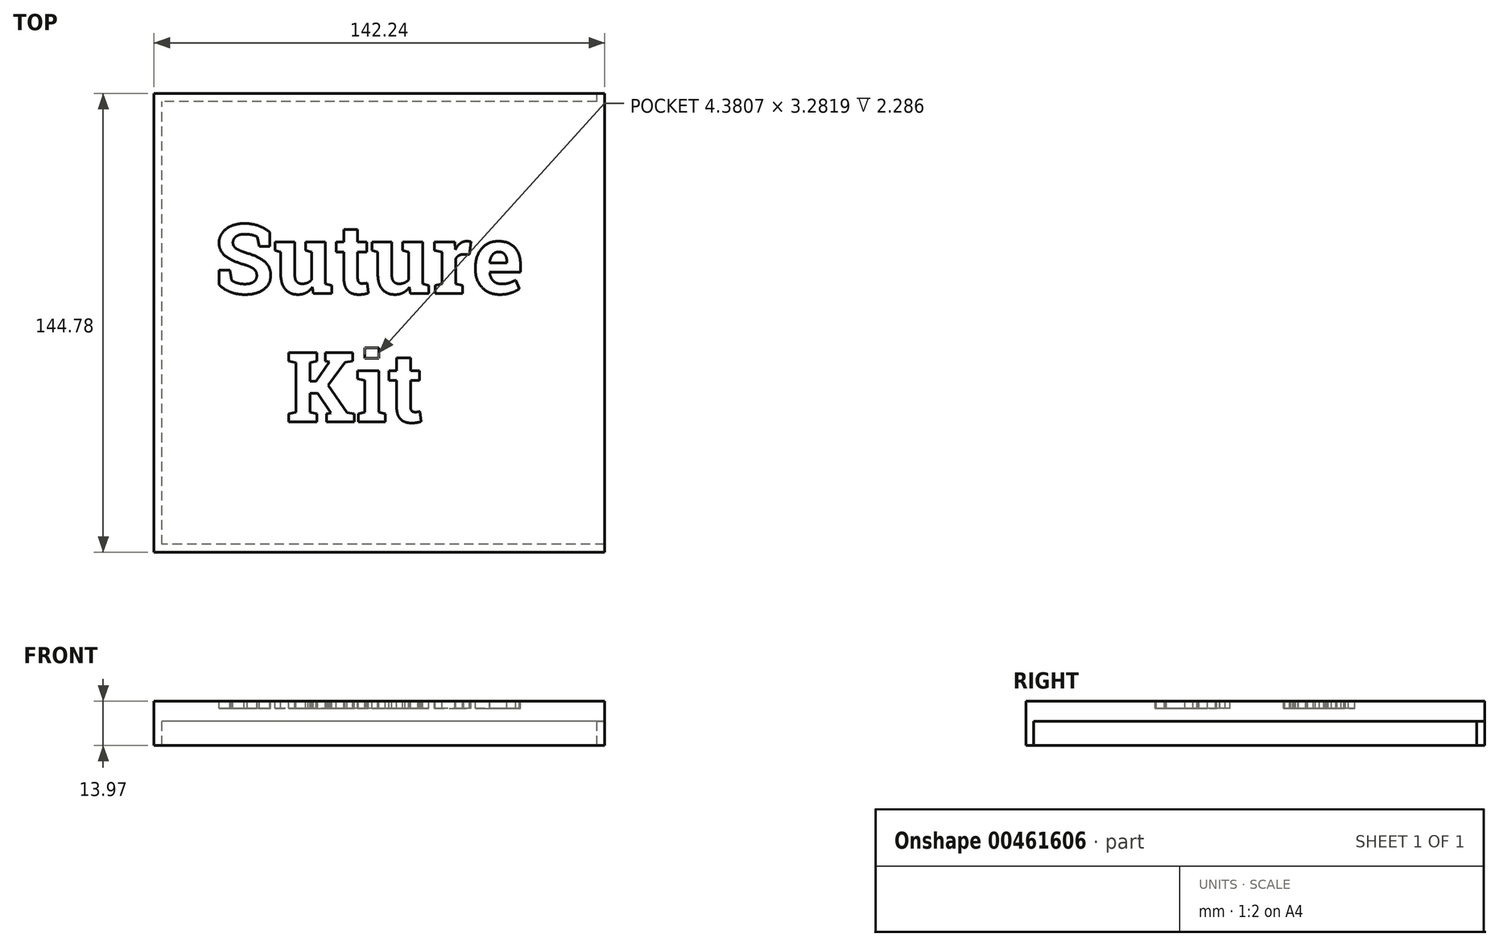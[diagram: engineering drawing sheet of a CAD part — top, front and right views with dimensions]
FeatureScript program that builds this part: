
annotation { "Feature Type Name" : "Feature", "Feature Type Description" : "" }
export const myFeature = defineFeature(function(context is Context, id is Id, definition is map)
    precondition{}
    {
        {
            var Q0;
            Q0=qCreatedBy(makeId("Top.planeOp"),FACE);
            var sketch = newSketch(context, id + "F0", { "sketchPlane" : qUnion([Q0])});
            skLineSegment(sketch, "E0.bottom", {"start": v(-68.3, 70.28) * mm, "end": v(73.93, 70.28) * mm});
            skLineSegment(sketch, "E0.top", {"start": v(-68.3, -74.5) * mm, "end": v(73.93, -74.5) * mm});
            skLineSegment(sketch, "E0.left", {"start": v(-68.3, 70.28) * mm, "end": v(-68.3, -74.5) * mm});
            skLineSegment(sketch, "E0.right", {"start": v(73.93, 70.28) * mm, "end": v(73.93, -74.5) * mm});
            skSolve(sketch);
        }
        {
            var Q0;
            Q0=makeQuery(id+"F0.imprint","IMPRINT",FACE,{"disambiguationData":[TD([[makeQuery(id+"F0.imprint","IMPRINT",EDGE,{"derivedFrom":sQuery(id+"F0.wireOp",EDGE,"E0.bottom")}),-1.0]])]});
            extrude(context, id + "F1", {"entities" : qUnion([Q0]), "depth" : 6.35 * mm});
        }
        {
            var Q0;
            Q0=makeQuery(id+"F1.opExtrude","CAP_FACE",FACE,{"disambiguationData":[OSD([sQuery(id+"F0.wireOp",EDGE,"E0.bottom"),sQuery(id+"F0.wireOp",EDGE,"E0.top"),sQuery(id+"F0.wireOp",EDGE,"E0.left"),sQuery(id+"F0.wireOp",EDGE,"E0.right")])],"isStart":true});
            var sketch = newSketch(context, id + "F2", { "sketchPlane" : qUnion([Q0])});
            skLineSegment(sketch, "E1.bottom", {"start": v(-68.3, 74.5) * mm, "end": v(-65.8, 74.5) * mm});
            skLineSegment(sketch, "E1.top", {"start": v(-68.3, -70.28) * mm, "end": v(-65.8, -70.28) * mm});
            skLineSegment(sketch, "E1.left", {"start": v(-68.3, 74.5) * mm, "end": v(-68.3, -70.28) * mm});
            skLineSegment(sketch, "E1.right", {"start": v(-65.8, 74.5) * mm, "end": v(-65.8, -70.28) * mm});
            skLineSegment(sketch, "E2.bottom", {"start": v(73.93, 74.5) * mm, "end": v(-65.8, 74.5) * mm});
            skLineSegment(sketch, "E2.top", {"start": v(73.93, 71.99) * mm, "end": v(-65.8, 71.99) * mm});
            skLineSegment(sketch, "E2.left", {"start": v(73.93, 74.5) * mm, "end": v(73.93, 71.99) * mm});
            skLineSegment(sketch, "E2.right", {"start": v(-65.8, 74.5) * mm, "end": v(-65.8, 71.99) * mm});
            skLineSegment(sketch, "E3.bottom", {"start": v(73.93, 71.99) * mm, "end": v(71.42, 71.99) * mm});
            skLineSegment(sketch, "E3.top", {"start": v(73.93, -70.28) * mm, "end": v(71.42, -70.28) * mm});
            skLineSegment(sketch, "E3.left", {"start": v(73.93, 71.99) * mm, "end": v(73.93, -70.28) * mm});
            skLineSegment(sketch, "E3.right", {"start": v(71.42, 71.99) * mm, "end": v(71.42, -70.28) * mm});
            skLineSegment(sketch, "E4.bottom", {"start": v(71.42, -70.28) * mm, "end": v(-65.8, -70.28) * mm});
            skLineSegment(sketch, "E4.top", {"start": v(71.42, -67.76) * mm, "end": v(-65.8, -67.76) * mm});
            skLineSegment(sketch, "E4.left", {"start": v(71.42, -70.28) * mm, "end": v(71.42, -67.76) * mm});
            skLineSegment(sketch, "E4.right", {"start": v(-65.8, -70.28) * mm, "end": v(-65.8, -67.76) * mm});
            skSolve(sketch);
        }
        {
            var Q0;
            Q0=makeQuery(id+"F2.imprint","IMPRINT",FACE,{"disambiguationData":[TD([[makeQuery(id+"F2.imprint","IMPRINT",EDGE,{"derivedFrom":sQuery(id+"F2.wireOp",EDGE,"E2.bottom")}),-1.0]])]});
            var Q1;
            Q1=makeQuery(id+"F2.imprint","IMPRINT",FACE,{"disambiguationData":[TD([[makeQuery(id+"F2.imprint","IMPRINT",EDGE,{"derivedFrom":sQuery(id+"F2.wireOp",EDGE,"E3.bottom")}),1.0]])]});
            var Q2;
            Q2=makeQuery(id+"F2.imprint","IMPRINT",FACE,{"disambiguationData":[TD([[makeQuery(id+"F2.imprint","IMPRINT",EDGE,{"derivedFrom":sQuery(id+"F2.wireOp",EDGE,"E1.bottom")}),-1.0]])]});
            var Q3;
            Q3=makeQuery(id+"F2.imprint","IMPRINT",FACE,{"disambiguationData":[TD([[makeQuery(id+"F2.imprint","IMPRINT",EDGE,{"derivedFrom":sQuery(id+"F2.wireOp",EDGE,"E4.bottom")}),1.0]])]});
            extrude(context, id + "F3", {"entities" : qUnion([Q0, Q1, Q2, Q3]), "operationType" : NewBodyOperationType.ADD, "depth" : 7.62 * mm});
        }
        {
            var Q0;
            Q0=makeQuery(id+"F1.opExtrude","CAP_FACE",FACE,{"disambiguationData":[OSD([sQuery(id+"F0.wireOp",EDGE,"E0.bottom"),sQuery(id+"F0.wireOp",EDGE,"E0.top"),sQuery(id+"F0.wireOp",EDGE,"E0.left"),sQuery(id+"F0.wireOp",EDGE,"E0.right")])],"isStart":false});
            var sketch = newSketch(context, id + "F4", { "sketchPlane" : qUnion([Q0])});
            skText(sketch, "E5", { "text": "Suture\n   Kit", "fontName": "RobotoSlab-Bold.ttf"});
            const initialGuessF4  = {"E5": [-0.04923, 0.00712, 1, 0, 0.02211]};
            skSetInitialGuess(sketch, initialGuessF4);
            skSolve(sketch);
        }
        {
            var Q0;
            Q0 = qSketchRegion(id + "F4", true);
            extrude(context, id + "F5", {"entities" : qUnion([Q0]), "operationType" : NewBodyOperationType.REMOVE, "oppositeDirection" : true, "depth" : 2.3 * mm});
        }
    });
